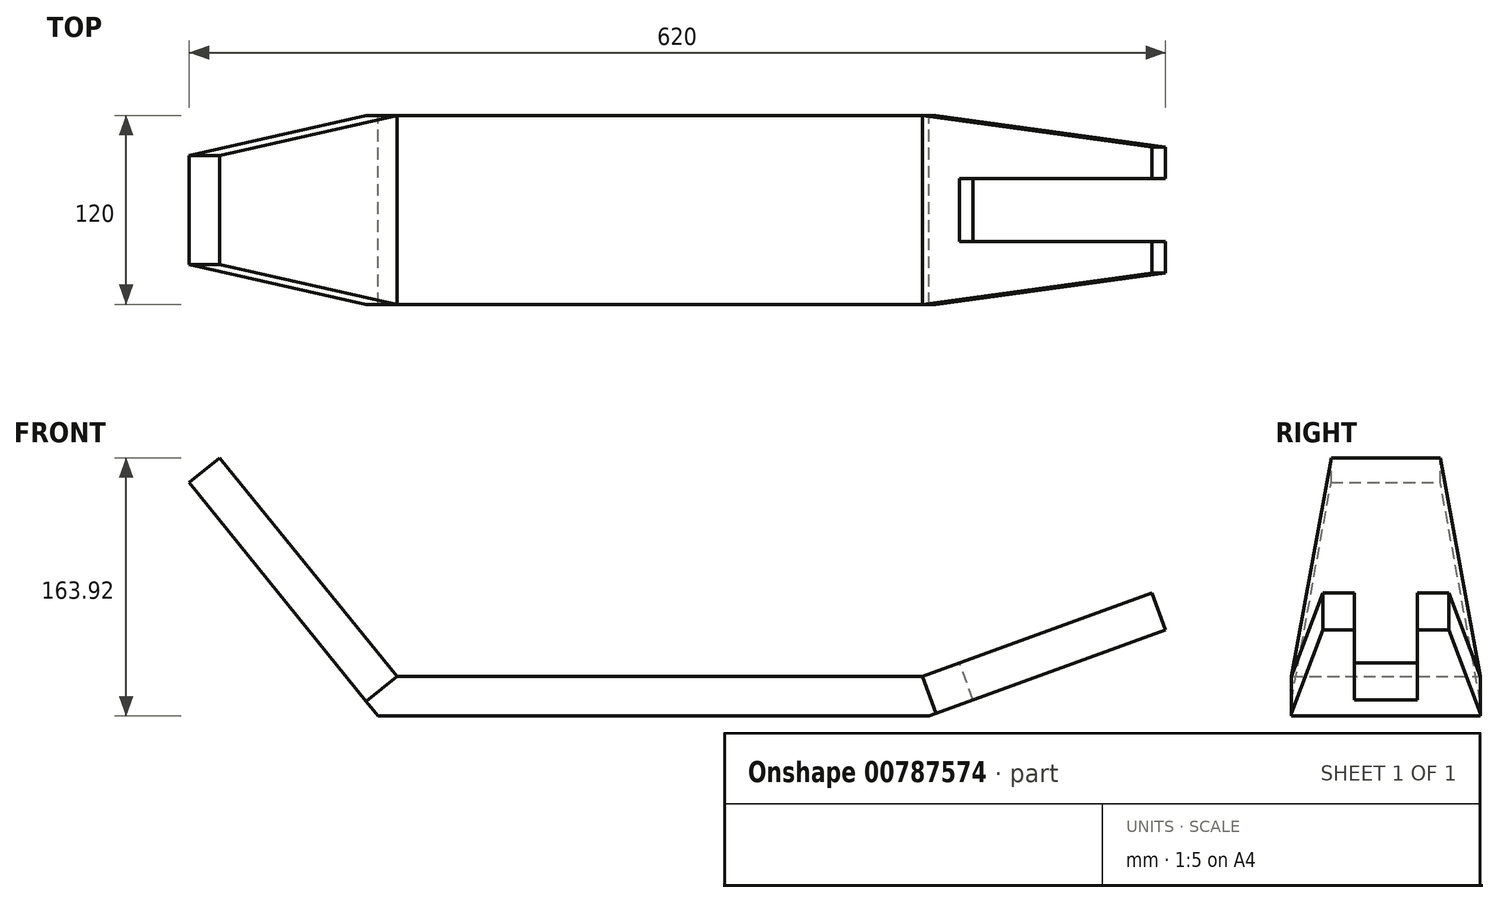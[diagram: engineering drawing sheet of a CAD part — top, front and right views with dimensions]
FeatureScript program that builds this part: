
annotation { "Feature Type Name" : "Feature", "Feature Type Description" : "" }
export const myFeature = defineFeature(function(context is Context, id is Id, definition is map)
    precondition{}
    {
        {
            var Q0;
            Q0=qCreatedBy(makeId("Front.planeOp"),FACE);
            var sketch = newSketch(context, id + "F0", { "sketchPlane" : qUnion([Q0])});
            skLineSegment(sketch, "E0", {"start": v(0, 0) * mm, "end": v(-120, 148.19) * mm});
            skLineSegment(sketch, "E1", {"start": v(0, 0) * mm, "end": v(350, 0) * mm});
            skLineSegment(sketch, "E2", {"start": v(350, 0) * mm, "end": v(500, 54.6) * mm});
            skLineSegment(sketch, "E3", {"start": v(350, 0) * mm, "end": v(500, 0) * mm, "construction": true});
            skLineSegment(sketch, "E4", {"start": v(500, 0) * mm, "end": v(500, 54.6) * mm, "construction": true});
            skLineSegment(sketch, "E5", {"start": v(-120, 148.19) * mm, "end": v(-120, 0) * mm, "construction": true});
            skLineSegment(sketch, "E6", {"start": v(-120, 0) * mm, "end": v(0, 0) * mm, "construction": true});
            skLineSegment(sketch, "E7.0", {"start": v(11.92, 25) * mm, "end": v(-100.57, 163.92) * mm});
            skLineSegment(sketch, "E7.1", {"start": v(11.92, 25) * mm, "end": v(345.6, 25) * mm});
            skLineSegment(sketch, "E7.2", {"start": v(345.6, 25) * mm, "end": v(491.45, 78.09) * mm});
            skLineSegment(sketch, "E8", {"start": v(-120, 148.19) * mm, "end": v(-100.57, 163.92) * mm});
            skLineSegment(sketch, "E9", {"start": v(491.45, 78.09) * mm, "end": v(500, 54.6) * mm});
            skSolve(sketch);
        }
        {
            var Q0;
            Q0=makeQuery(id+"F0.imprint","IMPRINT",FACE,{"disambiguationData":[TD([[makeQuery(id+"F0.imprint","IMPRINT",EDGE,{"derivedFrom":sQuery(id+"F0.wireOp",EDGE,"E0")}),-1.0]])]});
            extrude(context, id + "F1", {"entities" : qUnion([Q0]), "endBound" : BoundingType.SYMMETRIC, "depth" : 120 * mm, "offsetDistance" : 25 * mm});
        }
        {
            var Q0;
            Q0=makeQuery(id+"F1.opExtrude","SWEPT_FACE",FACE,{"disambiguationData":[OSD([sQuery(id+"F0.wireOp",EDGE,"E7.0")])]});
            var sketch = newSketch(context, id + "F2", { "sketchPlane" : qUnion([Q0])});
            skLineSegment(sketch, "E10", {"start": v(60, 11.92) * mm, "end": v(34.71, 190.68) * mm});
            skLineSegment(sketch, "E11", {"start": v(34.71, 190.68) * mm, "end": v(0, 190.68) * mm});
            skLineSegment(sketch, "E12", {"start": v(60, 11.92) * mm, "end": v(0, 11.92) * mm});
            skLineSegment(sketch, "E13.MirrorCS", {"start": v(-60, 11.92) * mm, "end": v(-34.71, 190.68) * mm});
            skLineSegment(sketch, "E14.MirrorCS", {"start": v(-60, 11.92) * mm, "end": v(0, 11.92) * mm});
            skLineSegment(sketch, "E15.MirrorCS", {"start": v(-34.71, 190.68) * mm, "end": v(0, 190.68) * mm});
            skSolve(sketch);
        }
        {
            var Q0;
            {var subQ0=sQuery(id+"F2.wireOp",EDGE,"E13.MirrorCS");Q0=makeQuery(id+"F2.imprint","IMPRINT",FACE,{"disambiguationData":[TD([[makeQuery(id+"F2.imprint","IMPRINT",EDGE,{"derivedFrom":subQ0}),1.0]])]});}
            var Q1;
            {var subQ0=sQuery(id+"F2.wireOp",EDGE,"E10");Q1=makeQuery(id+"F2.imprint","IMPRINT",FACE,{"disambiguationData":[TD([[makeQuery(id+"F2.imprint","IMPRINT",EDGE,{"derivedFrom":subQ0}),-1.0]])]});}
            extrude(context, id + "F3", {"entities" : qUnion([Q0, Q1]), "operationType" : NewBodyOperationType.REMOVE, "oppositeDirection" : true, "depth" : 25 * mm, "offsetDistance" : 25 * mm});
        }
        {
            var Q0;
            Q0=makeQuery(id+"F1.opExtrude","SWEPT_FACE",FACE,{"disambiguationData":[OSD([sQuery(id+"F0.wireOp",EDGE,"E7.2")])]});
            var sketch = newSketch(context, id + "F4", { "sketchPlane" : qUnion([Q0])});
            skLineSegment(sketch, "E16", {"start": v(333.3, -60) * mm, "end": v(488.52, -40) * mm});
            skLineSegment(sketch, "E17", {"start": v(488.52, -40) * mm, "end": v(488.52, -20) * mm});
            skLineSegment(sketch, "E18", {"start": v(488.52, -20) * mm, "end": v(358.52, -20) * mm});
            skLineSegment(sketch, "E19", {"start": v(358.52, -20) * mm, "end": v(358.52, 0) * mm});
            skLineSegment(sketch, "E20", {"start": v(333.3, -60) * mm, "end": v(333.3, 0) * mm});
            skLineSegment(sketch, "E21.MirrorCS", {"start": v(333.3, 60) * mm, "end": v(333.3, 0) * mm});
            skLineSegment(sketch, "E22.MirrorCS", {"start": v(358.52, 20) * mm, "end": v(358.52, 0) * mm});
            skLineSegment(sketch, "E23.MirrorCS", {"start": v(488.52, 40) * mm, "end": v(488.52, 20) * mm});
            skLineSegment(sketch, "E24.MirrorCS", {"start": v(488.52, 20) * mm, "end": v(358.52, 20) * mm});
            skLineSegment(sketch, "E25.MirrorCS", {"start": v(333.3, 60) * mm, "end": v(488.52, 40) * mm});
            skSolve(sketch);
        }
        {
            var Q0;
            {var subQ0=sQuery(id+"F4.wireOp",EDGE,"E25.MirrorCS");Q0=makeQuery(id+"F4.imprint","IMPRINT",FACE,{"disambiguationData":[TD([[makeQuery(id+"F4.imprint","IMPRINT",EDGE,{"derivedFrom":subQ0}),1.0]])]});}
            var Q1;
            {var subQ1=sQuery(id+"F4.wireOp",EDGE,"E18");Q1=makeQuery(id+"F4.imprint","IMPRINT",FACE,{"disambiguationData":[TD([[makeQuery(id+"F4.imprint","IMPRINT",EDGE,{"derivedFrom":subQ1}),-1.0]])]});}
            var Q2;
            {var subQ0=sQuery(id+"F4.wireOp",EDGE,"E16");Q2=makeQuery(id+"F4.imprint","IMPRINT",FACE,{"disambiguationData":[TD([[makeQuery(id+"F4.imprint","IMPRINT",EDGE,{"derivedFrom":subQ0}),-1.0]])]});}
            extrude(context, id + "F5", {"entities" : qUnion([Q0, Q1, Q2]), "operationType" : NewBodyOperationType.REMOVE, "oppositeDirection" : true, "depth" : 25 * mm, "offsetDistance" : 25 * mm});
        }
    });
